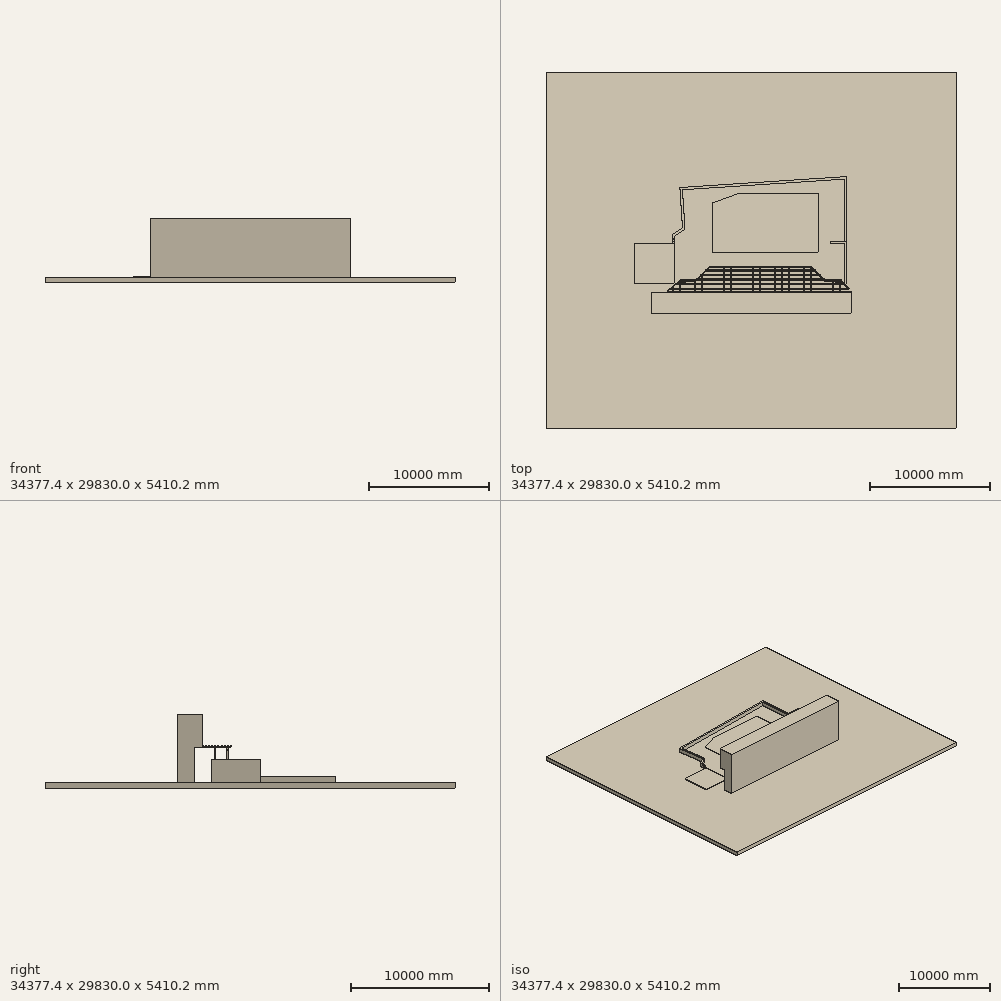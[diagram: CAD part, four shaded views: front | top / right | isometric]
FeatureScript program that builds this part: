
annotation { "Feature Type Name" : "Feature", "Feature Type Description" : "" }
export const myFeature = defineFeature(function(context is Context, id is Id, definition is map)
    precondition{}
    {
        {
            var Q0;
            Q0=qCreatedBy(makeId("Right.planeOp"),FACE);
            var sketch = newSketch(context, id + "F0", { "sketchPlane" : qUnion([Q0])});
            skLineSegment(sketch, "E0", {"start": v(0, 4953) * mm, "end": v(0, 0) * mm});
            skLineSegment(sketch, "E1", {"start": v(0, 4953) * mm, "end": v(1828.8, 4953) * mm});
            skLineSegment(sketch, "E2", {"start": v(1828.8, 4953) * mm, "end": v(1828.8, 2514.6) * mm});
            skLineSegment(sketch, "E3", {"start": v(1828.8, 2514.6) * mm, "end": v(1219.2, 2514.6) * mm});
            skLineSegment(sketch, "E4", {"start": v(1219.2, 2514.6) * mm, "end": v(1219.2, 0) * mm});
            skLineSegment(sketch, "E5", {"start": v(1219.2, 0) * mm, "end": v(0, 0) * mm});
            skSolve(sketch);
        }
        {
            var Q0;
            Q0 = qSketchRegion(id + "F0", true);
            extrude(context, id + "F1", {"entities" : qUnion([Q0]), "depth" : 16764 * mm, "offsetDistance" : 25.4 * mm});
        }
        {
            var Q0;
            Q0=qCreatedBy(makeId("Top.planeOp"),FACE);
            var sketch = newSketch(context, id + "F2", { "sketchPlane" : qUnion([Q0])});
            skLineSegment(sketch, "E6.bottom", {"start": v(-1422.4, 2540) * mm, "end": v(1930.4, 2540) * mm});
            skLineSegment(sketch, "E6.top", {"start": v(-1422.4, 5892.8) * mm, "end": v(1930.4, 5892.8) * mm});
            skLineSegment(sketch, "E6.left", {"start": v(-1422.4, 2540) * mm, "end": v(-1422.4, 5892.8) * mm});
            skLineSegment(sketch, "E6.right", {"start": v(1930.4, 2540) * mm, "end": v(1930.4, 5892.8) * mm});
            skSolve(sketch);
        }
        {
            var Q0;
            Q0 = qSketchRegion(id + "F2", true);
            extrude(context, id + "F3", {"entities" : qUnion([Q0]), "depth" : 76.2 * mm, "offsetDistance" : 25.4 * mm});
        }
        {
            var Q0;
            Q0=qCreatedBy(makeId("Top.planeOp"),FACE);
            var sketch = newSketch(context, id + "F4", { "sketchPlane" : qUnion([Q0])});
            skLineSegment(sketch, "E7", {"start": v(5130.8, 5130.8) * mm, "end": v(14020.8, 5130.8) * mm});
            skLineSegment(sketch, "E8", {"start": v(14020.8, 10109.2) * mm, "end": v(14020.8, 5130.8) * mm});
            skLineSegment(sketch, "E9", {"start": v(14020.8, 10109.2) * mm, "end": v(7375.8, 10109.2) * mm});
            skLineSegment(sketch, "E10", {"start": v(5130.8, 5130.8) * mm, "end": v(5130.8, 9296.4) * mm});
            skLineSegment(sketch, "E11", {"start": v(5130.8, 9296.4) * mm, "end": v(7375.8, 10109.2) * mm});
            skSolve(sketch);
        }
        {
            var Q0;
            Q0 = qSketchRegion(id + "F4", true);
            extrude(context, id + "F5", {"entities" : qUnion([Q0]), "depth" : 25.4 * mm, "offsetDistance" : 25.4 * mm});
        }
        {
            var Q0;
            Q0=qCreatedBy(makeId("Top.planeOp"),FACE);
            var sketch = newSketch(context, id + "F6", { "sketchPlane" : qUnion([Q0])});
            skLineSegment(sketch, "E12", {"start": v(15036.8, 6070.6) * mm, "end": v(15036.8, 5918.2) * mm});
            skLineSegment(sketch, "E13", {"start": v(15036.8, 5918.2) * mm, "end": v(16205.2, 5918.2) * mm});
            skLineSegment(sketch, "E14", {"start": v(16205.2, 5918.2) * mm, "end": v(16205.2, 2489.2) * mm});
            skLineSegment(sketch, "E15", {"start": v(16205.2, 2489.2) * mm, "end": v(16357.6, 2489.2) * mm});
            skLineSegment(sketch, "E16", {"start": v(16357.6, 2489.2) * mm, "end": v(16357.6, 6070.6) * mm});
            skLineSegment(sketch, "E17", {"start": v(16357.6, 6070.6) * mm, "end": v(15036.8, 6070.6) * mm});
            skSolve(sketch);
        }
        {
            var Q0;
            Q0 = qSketchRegion(id + "F6", true);
            extrude(context, id + "F7", {"entities" : qUnion([Q0]), "depth" : 1676.4 * mm, "offsetDistance" : 25.4 * mm});
        }
        {
            var Q0;
            Q0=qCreatedBy(makeId("Top.planeOp"),FACE);
            var sketch = newSketch(context, id + "F8", { "sketchPlane" : qUnion([Q0])});
            skLineSegment(sketch, "E18", {"start": v(1930.4, 5892.8) * mm, "end": v(1930.4, 6502.4) * mm});
            skLineSegment(sketch, "E19", {"start": v(1930.4, 6502.4) * mm, "end": v(2813.78, 7075.54) * mm});
            skLineSegment(sketch, "E20", {"start": v(2813.78, 7075.54) * mm, "end": v(2595.32, 10405.68) * mm});
            skLineSegment(sketch, "E21", {"start": v(2595.32, 10405.68) * mm, "end": v(16154.4, 11295.16) * mm});
            skLineSegment(sketch, "E22", {"start": v(16154.4, 11295.16) * mm, "end": v(16154.4, 6070.6) * mm});
            skLineSegment(sketch, "E23", {"start": v(16154.4, 6070.6) * mm, "end": v(16357.6, 6070.6) * mm});
            skLineSegment(sketch, "E24", {"start": v(16357.6, 6070.6) * mm, "end": v(16357.6, 11512.13) * mm});
            skLineSegment(sketch, "E25", {"start": v(16357.6, 11512.13) * mm, "end": v(2379.26, 10595.14) * mm});
            skLineSegment(sketch, "E26", {"start": v(2379.26, 10595.14) * mm, "end": v(2603.22, 7181.15) * mm});
            skLineSegment(sketch, "E27", {"start": v(2603.22, 7181.15) * mm, "end": v(1727.2, 6612.78) * mm});
            skLineSegment(sketch, "E28", {"start": v(1727.2, 6612.78) * mm, "end": v(1727.2, 5892.8) * mm});
            skLineSegment(sketch, "E29", {"start": v(1727.2, 5892.8) * mm, "end": v(1930.4, 5892.8) * mm});
            skSolve(sketch);
        }
        {
            var Q0;
            Q0 = qSketchRegion(id + "F8", true);
            extrude(context, id + "F9", {"entities" : qUnion([Q0]), "depth" : 457.2 * mm, "offsetDistance" : 25.4 * mm});
        }
        {
            var Q0;
            Q0=makeQuery(id+"F9.opExtrude","SWEPT_FACE",FACE,{"disambiguationData":[OSD([sQuery(id+"F8.wireOp",EDGE,"E18")])]});
            var sketch = newSketch(context, id + "F10", { "sketchPlane" : qUnion([Q0])});
            skLineSegment(sketch, "E30", {"start": v(5892.8, 114.3) * mm, "end": v(6045.2, 114.3) * mm});
            skLineSegment(sketch, "E31", {"start": v(6045.2, 114.3) * mm, "end": v(6045.2, 228.6) * mm});
            skLineSegment(sketch, "E32", {"start": v(6045.2, 228.6) * mm, "end": v(6197.6, 228.6) * mm});
            skLineSegment(sketch, "E33", {"start": v(6197.6, 228.6) * mm, "end": v(6197.6, 342.9) * mm});
            skLineSegment(sketch, "E34", {"start": v(6197.6, 342.9) * mm, "end": v(6350, 342.9) * mm});
            skLineSegment(sketch, "E35", {"start": v(6350, 342.9) * mm, "end": v(6350, 457.2) * mm});
            skLineSegment(sketch, "E36", {"start": v(6350, 457.2) * mm, "end": v(5892.8, 457.2) * mm});
            skLineSegment(sketch, "E37", {"start": v(5892.8, 457.2) * mm, "end": v(5892.8, 114.3) * mm});
            skSolve(sketch);
        }
        {
            var Q0;
            Q0 = qSketchRegion(id + "F10", true);
            extrude(context, id + "F11", {"entities" : qUnion([Q0]), "operationType" : NewBodyOperationType.REMOVE, "oppositeDirection" : true, "depth" : 203.2 * mm, "offsetDistance" : 25.4 * mm});
        }
        {
            var Q0;
            Q0=qCreatedBy(makeId("Top.planeOp"),FACE);
            var sketch = newSketch(context, id + "F12", { "sketchPlane" : qUnion([Q0])});
            skLineSegment(sketch, "E38.bottom", {"start": v(2590.8, 2667) * mm, "end": v(2692.4, 2667) * mm});
            skLineSegment(sketch, "E38.top", {"start": v(2590.8, 2768.6) * mm, "end": v(2692.4, 2768.6) * mm});
            skLineSegment(sketch, "E38.left", {"start": v(2590.8, 2667) * mm, "end": v(2590.8, 2768.6) * mm});
            skLineSegment(sketch, "E38.right", {"start": v(2692.4, 2667) * mm, "end": v(2692.4, 2768.6) * mm});
            skLineSegment(sketch, "E39.bottom", {"start": v(4826, 3581.4) * mm, "end": v(4927.6, 3581.4) * mm});
            skLineSegment(sketch, "E39.top", {"start": v(4826, 3683) * mm, "end": v(4927.6, 3683) * mm});
            skLineSegment(sketch, "E39.left", {"start": v(4826, 3683) * mm, "end": v(4826, 3581.4) * mm});
            skLineSegment(sketch, "E39.right", {"start": v(4927.6, 3683) * mm, "end": v(4927.6, 3581.4) * mm});
            skLineSegment(sketch, "E40.bottom", {"start": v(9093.2, 3683) * mm, "end": v(9194.8, 3683) * mm});
            skLineSegment(sketch, "E40.top", {"start": v(9093.2, 3581.4) * mm, "end": v(9194.8, 3581.4) * mm});
            skLineSegment(sketch, "E40.left", {"start": v(9093.2, 3683) * mm, "end": v(9093.2, 3581.4) * mm});
            skLineSegment(sketch, "E40.right", {"start": v(9194.8, 3683) * mm, "end": v(9194.8, 3581.4) * mm});
            skLineSegment(sketch, "E41", {"start": v(9144, 3250.57) * mm, "end": v(9144, 4336.45) * mm, "construction": true});
            skLineSegment(sketch, "E42.MirrorCS", {"start": v(13462, 3683) * mm, "end": v(13462, 3581.4) * mm});
            skLineSegment(sketch, "E43.MirrorCS", {"start": v(13360.4, 3683) * mm, "end": v(13360.4, 3581.4) * mm});
            skLineSegment(sketch, "E44.MirrorCS", {"start": v(13462, 3683) * mm, "end": v(13360.4, 3683) * mm});
            skLineSegment(sketch, "E45.MirrorCS", {"start": v(13462, 3581.4) * mm, "end": v(13360.4, 3581.4) * mm});
            skLineSegment(sketch, "E46.MirrorCS", {"start": v(15595.6, 2667) * mm, "end": v(15595.6, 2768.6) * mm});
            skLineSegment(sketch, "E47.MirrorCS", {"start": v(15697.2, 2768.6) * mm, "end": v(15595.6, 2768.6) * mm});
            skLineSegment(sketch, "E48.MirrorCS", {"start": v(15697.2, 2667) * mm, "end": v(15697.2, 2768.6) * mm});
            skLineSegment(sketch, "E49.MirrorCS", {"start": v(15697.2, 2667) * mm, "end": v(15595.6, 2667) * mm});
            skSolve(sketch);
        }
        {
            var Q0;
            Q0 = qSketchRegion(id + "F12", true);
            extrude(context, id + "F13", {"entities" : qUnion([Q0]), "depth" : 2336.8 * mm, "offsetDistance" : 25.4 * mm});
        }
        {
            var Q0;
            Q0=makeQuery(id+"F13.opExtrude","SWEPT_FACE",FACE,{"disambiguationData":[OSD([sQuery(id+"F12.wireOp",EDGE,"E40.bottom")])]});
            var sketch = newSketch(context, id + "F14", { "sketchPlane" : qUnion([Q0])});
            skLineSegment(sketch, "E50.bottom", {"start": v(-13665.2, 2514.6) * mm, "end": v(-4622.8, 2514.6) * mm});
            skLineSegment(sketch, "E50.top", {"start": v(-13576.3, 2336.8) * mm, "end": v(-4711.7, 2336.8) * mm});
            skLineSegment(sketch, "E50.left", {"start": v(-13665.2, 2514.6) * mm, "end": v(-13665.2, 2425.7) * mm});
            skLineSegment(sketch, "E50.right", {"start": v(-4622.8, 2514.6) * mm, "end": v(-4622.8, 2425.7) * mm});
            skLineSegment(sketch, "E51", {"start": v(-13665.2, 2425.7) * mm, "end": v(-13576.3, 2336.8) * mm});
            skPoint(sketch, "E52.orphan", {"position": v(-13665.2, 2336.8) * mm});
            skLineSegment(sketch, "E53", {"start": v(-4622.8, 2425.7) * mm, "end": v(-4711.7, 2336.8) * mm});
            skPoint(sketch, "E54.orphan", {"position": v(-4622.8, 2336.8) * mm});
            skSolve(sketch);
        }
        {
            var Q0;
            Q0 = qSketchRegion(id + "F14", true);
            extrude(context, id + "F15", {"entities" : qUnion([Q0]), "oppositeDirection" : true, "depth" : 101.6 * mm, "offsetDistance" : 25.4 * mm});
        }
        {
            var Q0;
            Q0=makeQuery(id+"F13.opExtrude","SWEPT_FACE",FACE,{"disambiguationData":[OSD([sQuery(id+"F12.wireOp",EDGE,"E38.top")])]});
            var sketch = newSketch(context, id + "F16", { "sketchPlane" : qUnion([Q0])});
            skLineSegment(sketch, "E55.bottom", {"start": v(-2895.6, 2514.6) * mm, "end": v(-2387.6, 2514.6) * mm});
            skLineSegment(sketch, "E55.top", {"start": v(-2806.7, 2336.8) * mm, "end": v(-2476.5, 2336.8) * mm});
            skLineSegment(sketch, "E55.left", {"start": v(-2895.6, 2514.6) * mm, "end": v(-2895.6, 2425.7) * mm});
            skLineSegment(sketch, "E55.right", {"start": v(-2387.6, 2514.6) * mm, "end": v(-2387.6, 2425.7) * mm});
            skLineSegment(sketch, "E56", {"start": v(-2895.6, 2425.7) * mm, "end": v(-2806.7, 2336.8) * mm});
            skLineSegment(sketch, "E57", {"start": v(-2387.6, 2425.7) * mm, "end": v(-2476.5, 2336.8) * mm});
            skPoint(sketch, "E58.orphan", {"position": v(-2895.6, 2336.8) * mm});
            skPoint(sketch, "E59.orphan", {"position": v(-2387.6, 2336.8) * mm});
            skLineSegment(sketch, "E60", {"start": v(-9144, 3615.2) * mm, "end": v(-9144, 519.06) * mm, "construction": true});
            skLineSegment(sketch, "E61.MirrorCS", {"start": v(-15392.4, 2514.6) * mm, "end": v(-15900.4, 2514.6) * mm});
            skLineSegment(sketch, "E62.MirrorCS", {"start": v(-15900.4, 2514.6) * mm, "end": v(-15900.4, 2425.7) * mm});
            skLineSegment(sketch, "E63.MirrorCS", {"start": v(-15900.4, 2425.7) * mm, "end": v(-15811.5, 2336.8) * mm});
            skLineSegment(sketch, "E64.MirrorCS", {"start": v(-15481.3, 2336.8) * mm, "end": v(-15811.5, 2336.8) * mm});
            skLineSegment(sketch, "E65.MirrorCS", {"start": v(-15392.4, 2425.7) * mm, "end": v(-15481.3, 2336.8) * mm});
            skLineSegment(sketch, "E66.MirrorCS", {"start": v(-15392.4, 2514.6) * mm, "end": v(-15392.4, 2425.7) * mm});
            skSolve(sketch);
        }
        {
            var Q0;
            Q0 = qSketchRegion(id + "F16", true);
            extrude(context, id + "F17", {"entities" : qUnion([Q0]), "oppositeDirection" : true, "depth" : 101.6 * mm, "offsetDistance" : 25.4 * mm});
        }
        {
            var Q0;
            Q0=makeQuery(id+"F1.opExtrude","SWEPT_FACE",FACE,{"disambiguationData":[OSD([sQuery(id+"F0.wireOp",EDGE,"E2")])]});
            var sketch = newSketch(context, id + "F18", { "sketchPlane" : qUnion([Q0])});
            skLineSegment(sketch, "E67.bottom", {"start": v(-16764, 2514.6) * mm, "end": v(-1320.8, 2514.6) * mm});
            skLineSegment(sketch, "E67.top", {"start": v(-16764, 2616.2) * mm, "end": v(-1320.8, 2616.2) * mm});
            skLineSegment(sketch, "E67.left", {"start": v(-16764, 2514.6) * mm, "end": v(-16764, 2616.2) * mm});
            skLineSegment(sketch, "E67.right", {"start": v(-1320.8, 2514.6) * mm, "end": v(-1320.8, 2616.2) * mm});
            skSolve(sketch);
        }
        {
            var Q0;
            Q0 = qSketchRegion(id + "F18", true);
            extrude(context, id + "F19", {"entities" : qUnion([Q0]), "operationType" : NewBodyOperationType.ADD, "depth" : 50.8 * mm, "offsetDistance" : 25.4 * mm});
        }
        {
            var Q0;
            Q0=makeQuery(id+"F15.opExtrude","SWEPT_FACE",FACE,{"disambiguationData":[OSD([sQuery(id+"F14.wireOp",EDGE,"E50.bottom")])]});
            var sketch = newSketch(context, id + "F20", { "sketchPlane" : qUnion([Q0])});
            skLineSegment(sketch, "E68", {"start": v(1320.8, 1879.6) * mm, "end": v(2387.6, 2768.6) * mm});
            skLineSegment(sketch, "E69", {"start": v(2387.6, 2768.6) * mm, "end": v(3708.4, 2768.6) * mm});
            skLineSegment(sketch, "E70", {"start": v(3708.4, 2768.6) * mm, "end": v(4902.2, 3962.4) * mm});
            skLineSegment(sketch, "E71", {"start": v(4902.2, 3962.4) * mm, "end": v(13385.8, 3962.4) * mm});
            skLineSegment(sketch, "E72", {"start": v(13385.8, 3962.4) * mm, "end": v(14579.6, 2768.6) * mm});
            skLineSegment(sketch, "E73", {"start": v(14579.6, 2768.6) * mm, "end": v(15900.4, 2768.6) * mm});
            skLineSegment(sketch, "E74", {"start": v(15900.4, 2768.6) * mm, "end": v(16764, 1879.6) * mm});
            skLineSegment(sketch, "E75", {"start": v(1320.8, 1879.6) * mm, "end": v(1400.15, 1879.6) * mm});
            skLineSegment(sketch, "E76", {"start": v(1400.15, 1879.6) * mm, "end": v(2406, 2717.8) * mm});
            skLineSegment(sketch, "E77", {"start": v(2406, 2717.8) * mm, "end": v(3729.44, 2717.8) * mm});
            skLineSegment(sketch, "E78", {"start": v(3729.44, 2717.8) * mm, "end": v(4923.24, 3911.6) * mm});
            skLineSegment(sketch, "E79", {"start": v(4923.24, 3911.6) * mm, "end": v(13364.76, 3911.6) * mm});
            skLineSegment(sketch, "E80", {"start": v(13364.76, 3911.6) * mm, "end": v(14558.56, 2717.8) * mm});
            skLineSegment(sketch, "E81", {"start": v(14558.56, 2717.8) * mm, "end": v(15878.93, 2717.8) * mm});
            skLineSegment(sketch, "E82", {"start": v(15878.93, 2717.8) * mm, "end": v(16693.18, 1879.6) * mm});
            skLineSegment(sketch, "E83", {"start": v(16693.18, 1879.6) * mm, "end": v(16764, 1879.6) * mm});
            skSolve(sketch);
        }
        {
            var Q0;
            Q0 = qSketchRegion(id + "F20", true);
            extrude(context, id + "F21", {"entities" : qUnion([Q0]), "depth" : 101.6 * mm, "offsetDistance" : 25.4 * mm});
        }
        {
            var Q0;
            Q0=makeQuery(id+"F19.opExtrude","CAP_FACE",FACE,{"disambiguationData":[OSD([sQuery(id+"F18.wireOp",EDGE,"E67.bottom"),sQuery(id+"F18.wireOp",EDGE,"E67.top"),sQuery(id+"F18.wireOp",EDGE,"E67.left"),sQuery(id+"F18.wireOp",EDGE,"E67.right")])],"isStart":false});
            var sketch = newSketch(context, id + "F22", { "sketchPlane" : qUnion([Q0])});
            skLineSegment(sketch, "E84.bottom", {"start": v(-1828.8, 2616.2) * mm, "end": v(-1778, 2616.2) * mm});
            skLineSegment(sketch, "E84.top", {"start": v(-1828.8, 2514.6) * mm, "end": v(-1778, 2514.6) * mm});
            skLineSegment(sketch, "E84.left", {"start": v(-1828.8, 2616.2) * mm, "end": v(-1828.8, 2514.6) * mm});
            skLineSegment(sketch, "E84.right", {"start": v(-1778, 2616.2) * mm, "end": v(-1778, 2514.6) * mm});
            skLineSegment(sketch, "E85.1.0.0", {"start": v(-2438.4, 2616.2) * mm, "end": v(-2438.4, 2514.6) * mm});
            skLineSegment(sketch, "E85.1.0.1", {"start": v(-2387.6, 2616.2) * mm, "end": v(-2387.6, 2514.6) * mm});
            skLineSegment(sketch, "E85.1.0.2", {"start": v(-2438.4, 2616.2) * mm, "end": v(-2387.6, 2616.2) * mm});
            skLineSegment(sketch, "E85.1.0.3", {"start": v(-2438.4, 2514.6) * mm, "end": v(-2387.6, 2514.6) * mm});
            skLineSegment(sketch, "E85.2.0.0", {"start": v(-3048, 2616.2) * mm, "end": v(-3048, 2514.6) * mm});
            skLineSegment(sketch, "E85.2.0.1", {"start": v(-2997.2, 2616.2) * mm, "end": v(-2997.2, 2514.6) * mm});
            skLineSegment(sketch, "E85.2.0.2", {"start": v(-3048, 2616.2) * mm, "end": v(-2997.2, 2616.2) * mm});
            skLineSegment(sketch, "E85.2.0.3", {"start": v(-3048, 2514.6) * mm, "end": v(-2997.2, 2514.6) * mm});
            skLineSegment(sketch, "E85.3.0.0", {"start": v(-3657.6, 2616.2) * mm, "end": v(-3657.6, 2514.6) * mm});
            skLineSegment(sketch, "E85.3.0.1", {"start": v(-3606.8, 2616.2) * mm, "end": v(-3606.8, 2514.6) * mm});
            skLineSegment(sketch, "E85.3.0.2", {"start": v(-3657.6, 2616.2) * mm, "end": v(-3606.8, 2616.2) * mm});
            skLineSegment(sketch, "E85.3.0.3", {"start": v(-3657.6, 2514.6) * mm, "end": v(-3606.8, 2514.6) * mm});
            skLineSegment(sketch, "E85.4.0.0", {"start": v(-4267.2, 2616.2) * mm, "end": v(-4267.2, 2514.6) * mm});
            skLineSegment(sketch, "E85.4.0.1", {"start": v(-4216.4, 2616.2) * mm, "end": v(-4216.4, 2514.6) * mm});
            skLineSegment(sketch, "E85.4.0.2", {"start": v(-4267.2, 2616.2) * mm, "end": v(-4216.4, 2616.2) * mm});
            skLineSegment(sketch, "E85.4.0.3", {"start": v(-4267.2, 2514.6) * mm, "end": v(-4216.4, 2514.6) * mm});
            skLineSegment(sketch, "E85.5.0.0", {"start": v(-4876.8, 2616.2) * mm, "end": v(-4876.8, 2514.6) * mm});
            skLineSegment(sketch, "E85.5.0.1", {"start": v(-4826, 2616.2) * mm, "end": v(-4826, 2514.6) * mm});
            skLineSegment(sketch, "E85.5.0.2", {"start": v(-4876.8, 2616.2) * mm, "end": v(-4826, 2616.2) * mm});
            skLineSegment(sketch, "E85.5.0.3", {"start": v(-4876.8, 2514.6) * mm, "end": v(-4826, 2514.6) * mm});
            skLineSegment(sketch, "E85.6.0.0", {"start": v(-5486.4, 2616.2) * mm, "end": v(-5486.4, 2514.6) * mm});
            skLineSegment(sketch, "E85.6.0.1", {"start": v(-5435.6, 2616.2) * mm, "end": v(-5435.6, 2514.6) * mm});
            skLineSegment(sketch, "E85.6.0.2", {"start": v(-5486.4, 2616.2) * mm, "end": v(-5435.6, 2616.2) * mm});
            skLineSegment(sketch, "E85.6.0.3", {"start": v(-5486.4, 2514.6) * mm, "end": v(-5435.6, 2514.6) * mm});
            skLineSegment(sketch, "E85.7.0.0", {"start": v(-6096, 2616.2) * mm, "end": v(-6096, 2514.6) * mm});
            skLineSegment(sketch, "E85.7.0.1", {"start": v(-6045.2, 2616.2) * mm, "end": v(-6045.2, 2514.6) * mm});
            skLineSegment(sketch, "E85.7.0.2", {"start": v(-6096, 2616.2) * mm, "end": v(-6045.2, 2616.2) * mm});
            skLineSegment(sketch, "E85.7.0.3", {"start": v(-6096, 2514.6) * mm, "end": v(-6045.2, 2514.6) * mm});
            skLineSegment(sketch, "E85.8.0.0", {"start": v(-6705.6, 2616.2) * mm, "end": v(-6705.6, 2514.6) * mm});
            skLineSegment(sketch, "E85.8.0.1", {"start": v(-6654.8, 2616.2) * mm, "end": v(-6654.8, 2514.6) * mm});
            skLineSegment(sketch, "E85.8.0.2", {"start": v(-6705.6, 2616.2) * mm, "end": v(-6654.8, 2616.2) * mm});
            skLineSegment(sketch, "E85.8.0.3", {"start": v(-6705.6, 2514.6) * mm, "end": v(-6654.8, 2514.6) * mm});
            skLineSegment(sketch, "E85.9.0.0", {"start": v(-7315.2, 2616.2) * mm, "end": v(-7315.2, 2514.6) * mm});
            skLineSegment(sketch, "E85.9.0.1", {"start": v(-7264.4, 2616.2) * mm, "end": v(-7264.4, 2514.6) * mm});
            skLineSegment(sketch, "E85.9.0.2", {"start": v(-7315.2, 2616.2) * mm, "end": v(-7264.4, 2616.2) * mm});
            skLineSegment(sketch, "E85.9.0.3", {"start": v(-7315.2, 2514.6) * mm, "end": v(-7264.4, 2514.6) * mm});
            skLineSegment(sketch, "E85.10.0.0", {"start": v(-7924.8, 2616.2) * mm, "end": v(-7924.8, 2514.6) * mm});
            skLineSegment(sketch, "E85.10.0.1", {"start": v(-7874, 2616.2) * mm, "end": v(-7874, 2514.6) * mm});
            skLineSegment(sketch, "E85.10.0.2", {"start": v(-7924.8, 2616.2) * mm, "end": v(-7874, 2616.2) * mm});
            skLineSegment(sketch, "E85.10.0.3", {"start": v(-7924.8, 2514.6) * mm, "end": v(-7874, 2514.6) * mm});
            skLineSegment(sketch, "E85.11.0.0", {"start": v(-8534.4, 2616.2) * mm, "end": v(-8534.4, 2514.6) * mm});
            skLineSegment(sketch, "E85.11.0.1", {"start": v(-8483.6, 2616.2) * mm, "end": v(-8483.6, 2514.6) * mm});
            skLineSegment(sketch, "E85.11.0.2", {"start": v(-8534.4, 2616.2) * mm, "end": v(-8483.6, 2616.2) * mm});
            skLineSegment(sketch, "E85.11.0.3", {"start": v(-8534.4, 2514.6) * mm, "end": v(-8483.6, 2514.6) * mm});
            skLineSegment(sketch, "E85.12.0.0", {"start": v(-9144, 2616.2) * mm, "end": v(-9144, 2514.6) * mm});
            skLineSegment(sketch, "E85.12.0.1", {"start": v(-9093.2, 2616.2) * mm, "end": v(-9093.2, 2514.6) * mm});
            skLineSegment(sketch, "E85.12.0.2", {"start": v(-9144, 2616.2) * mm, "end": v(-9093.2, 2616.2) * mm});
            skLineSegment(sketch, "E85.12.0.3", {"start": v(-9144, 2514.6) * mm, "end": v(-9093.2, 2514.6) * mm});
            skLineSegment(sketch, "E85.13.0.0", {"start": v(-9753.6, 2616.2) * mm, "end": v(-9753.6, 2514.6) * mm});
            skLineSegment(sketch, "E85.13.0.1", {"start": v(-9702.8, 2616.2) * mm, "end": v(-9702.8, 2514.6) * mm});
            skLineSegment(sketch, "E85.13.0.2", {"start": v(-9753.6, 2616.2) * mm, "end": v(-9702.8, 2616.2) * mm});
            skLineSegment(sketch, "E85.13.0.3", {"start": v(-9753.6, 2514.6) * mm, "end": v(-9702.8, 2514.6) * mm});
            skLineSegment(sketch, "E85.14.0.0", {"start": v(-10363.2, 2616.2) * mm, "end": v(-10363.2, 2514.6) * mm});
            skLineSegment(sketch, "E85.14.0.1", {"start": v(-10312.4, 2616.2) * mm, "end": v(-10312.4, 2514.6) * mm});
            skLineSegment(sketch, "E85.14.0.2", {"start": v(-10363.2, 2616.2) * mm, "end": v(-10312.4, 2616.2) * mm});
            skLineSegment(sketch, "E85.14.0.3", {"start": v(-10363.2, 2514.6) * mm, "end": v(-10312.4, 2514.6) * mm});
            skLineSegment(sketch, "E85.15.0.0", {"start": v(-10972.8, 2616.2) * mm, "end": v(-10972.8, 2514.6) * mm});
            skLineSegment(sketch, "E85.15.0.1", {"start": v(-10922, 2616.2) * mm, "end": v(-10922, 2514.6) * mm});
            skLineSegment(sketch, "E85.15.0.2", {"start": v(-10972.8, 2616.2) * mm, "end": v(-10922, 2616.2) * mm});
            skLineSegment(sketch, "E85.15.0.3", {"start": v(-10972.8, 2514.6) * mm, "end": v(-10922, 2514.6) * mm});
            skLineSegment(sketch, "E85.16.0.0", {"start": v(-11582.4, 2616.2) * mm, "end": v(-11582.4, 2514.6) * mm});
            skLineSegment(sketch, "E85.16.0.1", {"start": v(-11531.6, 2616.2) * mm, "end": v(-11531.6, 2514.6) * mm});
            skLineSegment(sketch, "E85.16.0.2", {"start": v(-11582.4, 2616.2) * mm, "end": v(-11531.6, 2616.2) * mm});
            skLineSegment(sketch, "E85.16.0.3", {"start": v(-11582.4, 2514.6) * mm, "end": v(-11531.6, 2514.6) * mm});
            skLineSegment(sketch, "E85.17.0.0", {"start": v(-12192, 2616.2) * mm, "end": v(-12192, 2514.6) * mm});
            skLineSegment(sketch, "E85.17.0.1", {"start": v(-12141.2, 2616.2) * mm, "end": v(-12141.2, 2514.6) * mm});
            skLineSegment(sketch, "E85.17.0.2", {"start": v(-12192, 2616.2) * mm, "end": v(-12141.2, 2616.2) * mm});
            skLineSegment(sketch, "E85.17.0.3", {"start": v(-12192, 2514.6) * mm, "end": v(-12141.2, 2514.6) * mm});
            skLineSegment(sketch, "E85.18.0.0", {"start": v(-12801.6, 2616.2) * mm, "end": v(-12801.6, 2514.6) * mm});
            skLineSegment(sketch, "E85.18.0.1", {"start": v(-12750.8, 2616.2) * mm, "end": v(-12750.8, 2514.6) * mm});
            skLineSegment(sketch, "E85.18.0.2", {"start": v(-12801.6, 2616.2) * mm, "end": v(-12750.8, 2616.2) * mm});
            skLineSegment(sketch, "E85.18.0.3", {"start": v(-12801.6, 2514.6) * mm, "end": v(-12750.8, 2514.6) * mm});
            skLineSegment(sketch, "E85.19.0.0", {"start": v(-13411.2, 2616.2) * mm, "end": v(-13411.2, 2514.6) * mm});
            skLineSegment(sketch, "E85.19.0.1", {"start": v(-13360.4, 2616.2) * mm, "end": v(-13360.4, 2514.6) * mm});
            skLineSegment(sketch, "E85.19.0.2", {"start": v(-13411.2, 2616.2) * mm, "end": v(-13360.4, 2616.2) * mm});
            skLineSegment(sketch, "E85.19.0.3", {"start": v(-13411.2, 2514.6) * mm, "end": v(-13360.4, 2514.6) * mm});
            skLineSegment(sketch, "E85.20.0.0", {"start": v(-14020.8, 2616.2) * mm, "end": v(-14020.8, 2514.6) * mm});
            skLineSegment(sketch, "E85.20.0.1", {"start": v(-13970, 2616.2) * mm, "end": v(-13970, 2514.6) * mm});
            skLineSegment(sketch, "E85.20.0.2", {"start": v(-14020.8, 2616.2) * mm, "end": v(-13970, 2616.2) * mm});
            skLineSegment(sketch, "E85.20.0.3", {"start": v(-14020.8, 2514.6) * mm, "end": v(-13970, 2514.6) * mm});
            skLineSegment(sketch, "E85.21.0.0", {"start": v(-14630.4, 2616.2) * mm, "end": v(-14630.4, 2514.6) * mm});
            skLineSegment(sketch, "E85.21.0.1", {"start": v(-14579.6, 2616.2) * mm, "end": v(-14579.6, 2514.6) * mm});
            skLineSegment(sketch, "E85.21.0.2", {"start": v(-14630.4, 2616.2) * mm, "end": v(-14579.6, 2616.2) * mm});
            skLineSegment(sketch, "E85.21.0.3", {"start": v(-14630.4, 2514.6) * mm, "end": v(-14579.6, 2514.6) * mm});
            skLineSegment(sketch, "E85.22.0.0", {"start": v(-15240, 2616.2) * mm, "end": v(-15240, 2514.6) * mm});
            skLineSegment(sketch, "E85.22.0.1", {"start": v(-15189.2, 2616.2) * mm, "end": v(-15189.2, 2514.6) * mm});
            skLineSegment(sketch, "E85.22.0.2", {"start": v(-15240, 2616.2) * mm, "end": v(-15189.2, 2616.2) * mm});
            skLineSegment(sketch, "E85.22.0.3", {"start": v(-15240, 2514.6) * mm, "end": v(-15189.2, 2514.6) * mm});
            skLineSegment(sketch, "E85.23.0.0", {"start": v(-15849.6, 2616.2) * mm, "end": v(-15849.6, 2514.6) * mm});
            skLineSegment(sketch, "E85.23.0.1", {"start": v(-15798.8, 2616.2) * mm, "end": v(-15798.8, 2514.6) * mm});
            skLineSegment(sketch, "E85.23.0.2", {"start": v(-15849.6, 2616.2) * mm, "end": v(-15798.8, 2616.2) * mm});
            skLineSegment(sketch, "E85.23.0.3", {"start": v(-15849.6, 2514.6) * mm, "end": v(-15798.8, 2514.6) * mm});
            skLineSegment(sketch, "E85.24.0.0", {"start": v(-16459.2, 2616.2) * mm, "end": v(-16459.2, 2514.6) * mm});
            skLineSegment(sketch, "E85.24.0.1", {"start": v(-16408.4, 2616.2) * mm, "end": v(-16408.4, 2514.6) * mm});
            skLineSegment(sketch, "E85.24.0.2", {"start": v(-16459.2, 2616.2) * mm, "end": v(-16408.4, 2616.2) * mm});
            skLineSegment(sketch, "E85.24.0.3", {"start": v(-16459.2, 2514.6) * mm, "end": v(-16408.4, 2514.6) * mm});
            skLineSegment(sketch, "E85.direction1", {"start": v(-1828.8, 2514.6) * mm, "end": v(-2438.4, 2514.6) * mm, "construction": true});
            skSolve(sketch);
        }
        {
            var Q0;
            Q0 = qSketchRegion(id + "F22", true);
            extrude(context, id + "F23", {"entities" : qUnion([Q0]), "endBound" : BoundingType.UP_TO_NEXT, "depth" : 25.4 * mm, "offsetDistance" : 25.4 * mm});
        }
        {
            var Q0;
            Q0=makeQuery(id+"F19.boolean.opBoolean","MERGE",FACE,{"derivedFrom":[makeQuery(id+"F1.opExtrude","CAP_FACE",FACE,{"disambiguationData":[OSD([sQuery(id+"F0.wireOp",EDGE,"E0"),sQuery(id+"F0.wireOp",EDGE,"E1"),sQuery(id+"F0.wireOp",EDGE,"E2"),sQuery(id+"F0.wireOp",EDGE,"E3"),sQuery(id+"F0.wireOp",EDGE,"E4"),sQuery(id+"F0.wireOp",EDGE,"E5")])],"isStart":false}),makeQuery(id+"F19.opExtrude","SWEPT_FACE",FACE,{"disambiguationData":[OSD([sQuery(id+"F18.wireOp",EDGE,"E67.left")])]})]});
            var sketch = newSketch(context, id + "F24", { "sketchPlane" : qUnion([Q0])});
            skLineSegment(sketch, "E86.bottom", {"start": v(1854.2, 2667) * mm, "end": v(1884.68, 2667) * mm});
            skLineSegment(sketch, "E86.top", {"start": v(1854.2, 2616.2) * mm, "end": v(1884.68, 2616.2) * mm});
            skLineSegment(sketch, "E86.left", {"start": v(1854.2, 2667) * mm, "end": v(1854.2, 2616.2) * mm});
            skLineSegment(sketch, "E86.right", {"start": v(1884.68, 2667) * mm, "end": v(1884.68, 2616.2) * mm});
            skLineSegment(sketch, "E87.1.0.0", {"start": v(1960.88, 2616.2) * mm, "end": v(1991.36, 2616.2) * mm});
            skLineSegment(sketch, "E87.1.0.1", {"start": v(1991.36, 2667) * mm, "end": v(1991.36, 2616.2) * mm});
            skLineSegment(sketch, "E87.1.0.2", {"start": v(1960.88, 2667) * mm, "end": v(1991.36, 2667) * mm});
            skLineSegment(sketch, "E87.1.0.3", {"start": v(1960.88, 2667) * mm, "end": v(1960.88, 2616.2) * mm});
            skLineSegment(sketch, "E87.2.0.0", {"start": v(2067.56, 2616.2) * mm, "end": v(2098.04, 2616.2) * mm});
            skLineSegment(sketch, "E87.2.0.1", {"start": v(2098.04, 2667) * mm, "end": v(2098.04, 2616.2) * mm});
            skLineSegment(sketch, "E87.2.0.2", {"start": v(2067.56, 2667) * mm, "end": v(2098.04, 2667) * mm});
            skLineSegment(sketch, "E87.2.0.3", {"start": v(2067.56, 2667) * mm, "end": v(2067.56, 2616.2) * mm});
            skLineSegment(sketch, "E87.3.0.0", {"start": v(2174.24, 2616.2) * mm, "end": v(2204.72, 2616.2) * mm});
            skLineSegment(sketch, "E87.3.0.1", {"start": v(2204.72, 2667) * mm, "end": v(2204.72, 2616.2) * mm});
            skLineSegment(sketch, "E87.3.0.2", {"start": v(2174.24, 2667) * mm, "end": v(2204.72, 2667) * mm});
            skLineSegment(sketch, "E87.3.0.3", {"start": v(2174.24, 2667) * mm, "end": v(2174.24, 2616.2) * mm});
            skLineSegment(sketch, "E87.4.0.0", {"start": v(2280.92, 2616.2) * mm, "end": v(2311.4, 2616.2) * mm});
            skLineSegment(sketch, "E87.4.0.1", {"start": v(2311.4, 2667) * mm, "end": v(2311.4, 2616.2) * mm});
            skLineSegment(sketch, "E87.4.0.2", {"start": v(2280.92, 2667) * mm, "end": v(2311.4, 2667) * mm});
            skLineSegment(sketch, "E87.4.0.3", {"start": v(2280.92, 2667) * mm, "end": v(2280.92, 2616.2) * mm});
            skLineSegment(sketch, "E87.5.0.0", {"start": v(2387.6, 2616.2) * mm, "end": v(2418.08, 2616.2) * mm});
            skLineSegment(sketch, "E87.5.0.1", {"start": v(2418.08, 2667) * mm, "end": v(2418.08, 2616.2) * mm});
            skLineSegment(sketch, "E87.5.0.2", {"start": v(2387.6, 2667) * mm, "end": v(2418.08, 2667) * mm});
            skLineSegment(sketch, "E87.5.0.3", {"start": v(2387.6, 2667) * mm, "end": v(2387.6, 2616.2) * mm});
            skLineSegment(sketch, "E87.6.0.0", {"start": v(2494.28, 2616.2) * mm, "end": v(2524.76, 2616.2) * mm});
            skLineSegment(sketch, "E87.6.0.1", {"start": v(2524.76, 2667) * mm, "end": v(2524.76, 2616.2) * mm});
            skLineSegment(sketch, "E87.6.0.2", {"start": v(2494.28, 2667) * mm, "end": v(2524.76, 2667) * mm});
            skLineSegment(sketch, "E87.6.0.3", {"start": v(2494.28, 2667) * mm, "end": v(2494.28, 2616.2) * mm});
            skLineSegment(sketch, "E87.7.0.0", {"start": v(2600.96, 2616.2) * mm, "end": v(2631.44, 2616.2) * mm});
            skLineSegment(sketch, "E87.7.0.1", {"start": v(2631.44, 2667) * mm, "end": v(2631.44, 2616.2) * mm});
            skLineSegment(sketch, "E87.7.0.2", {"start": v(2600.96, 2667) * mm, "end": v(2631.44, 2667) * mm});
            skLineSegment(sketch, "E87.7.0.3", {"start": v(2600.96, 2667) * mm, "end": v(2600.96, 2616.2) * mm});
            skLineSegment(sketch, "E87.8.0.0", {"start": v(2707.64, 2616.2) * mm, "end": v(2738.12, 2616.2) * mm});
            skLineSegment(sketch, "E87.8.0.1", {"start": v(2738.12, 2667) * mm, "end": v(2738.12, 2616.2) * mm});
            skLineSegment(sketch, "E87.8.0.2", {"start": v(2707.64, 2667) * mm, "end": v(2738.12, 2667) * mm});
            skLineSegment(sketch, "E87.8.0.3", {"start": v(2707.64, 2667) * mm, "end": v(2707.64, 2616.2) * mm});
            skLineSegment(sketch, "E87.9.0.0", {"start": v(2814.32, 2616.2) * mm, "end": v(2844.8, 2616.2) * mm});
            skLineSegment(sketch, "E87.9.0.1", {"start": v(2844.8, 2667) * mm, "end": v(2844.8, 2616.2) * mm});
            skLineSegment(sketch, "E87.9.0.2", {"start": v(2814.32, 2667) * mm, "end": v(2844.8, 2667) * mm});
            skLineSegment(sketch, "E87.9.0.3", {"start": v(2814.32, 2667) * mm, "end": v(2814.32, 2616.2) * mm});
            skLineSegment(sketch, "E87.10.0.0", {"start": v(2921, 2616.2) * mm, "end": v(2951.48, 2616.2) * mm});
            skLineSegment(sketch, "E87.10.0.1", {"start": v(2951.48, 2667) * mm, "end": v(2951.48, 2616.2) * mm});
            skLineSegment(sketch, "E87.10.0.2", {"start": v(2921, 2667) * mm, "end": v(2951.48, 2667) * mm});
            skLineSegment(sketch, "E87.10.0.3", {"start": v(2921, 2667) * mm, "end": v(2921, 2616.2) * mm});
            skLineSegment(sketch, "E87.11.0.0", {"start": v(3027.68, 2616.2) * mm, "end": v(3058.16, 2616.2) * mm});
            skLineSegment(sketch, "E87.11.0.1", {"start": v(3058.16, 2667) * mm, "end": v(3058.16, 2616.2) * mm});
            skLineSegment(sketch, "E87.11.0.2", {"start": v(3027.68, 2667) * mm, "end": v(3058.16, 2667) * mm});
            skLineSegment(sketch, "E87.11.0.3", {"start": v(3027.68, 2667) * mm, "end": v(3027.68, 2616.2) * mm});
            skLineSegment(sketch, "E87.12.0.0", {"start": v(3134.36, 2616.2) * mm, "end": v(3164.84, 2616.2) * mm});
            skLineSegment(sketch, "E87.12.0.1", {"start": v(3164.84, 2667) * mm, "end": v(3164.84, 2616.2) * mm});
            skLineSegment(sketch, "E87.12.0.2", {"start": v(3134.36, 2667) * mm, "end": v(3164.84, 2667) * mm});
            skLineSegment(sketch, "E87.12.0.3", {"start": v(3134.36, 2667) * mm, "end": v(3134.36, 2616.2) * mm});
            skLineSegment(sketch, "E87.13.0.0", {"start": v(3241.04, 2616.2) * mm, "end": v(3271.52, 2616.2) * mm});
            skLineSegment(sketch, "E87.13.0.1", {"start": v(3271.52, 2667) * mm, "end": v(3271.52, 2616.2) * mm});
            skLineSegment(sketch, "E87.13.0.2", {"start": v(3241.04, 2667) * mm, "end": v(3271.52, 2667) * mm});
            skLineSegment(sketch, "E87.13.0.3", {"start": v(3241.04, 2667) * mm, "end": v(3241.04, 2616.2) * mm});
            skLineSegment(sketch, "E87.14.0.0", {"start": v(3347.72, 2616.2) * mm, "end": v(3378.2, 2616.2) * mm});
            skLineSegment(sketch, "E87.14.0.1", {"start": v(3378.2, 2667) * mm, "end": v(3378.2, 2616.2) * mm});
            skLineSegment(sketch, "E87.14.0.2", {"start": v(3347.72, 2667) * mm, "end": v(3378.2, 2667) * mm});
            skLineSegment(sketch, "E87.14.0.3", {"start": v(3347.72, 2667) * mm, "end": v(3347.72, 2616.2) * mm});
            skLineSegment(sketch, "E87.15.0.0", {"start": v(3454.4, 2616.2) * mm, "end": v(3484.88, 2616.2) * mm});
            skLineSegment(sketch, "E87.15.0.1", {"start": v(3484.88, 2667) * mm, "end": v(3484.88, 2616.2) * mm});
            skLineSegment(sketch, "E87.15.0.2", {"start": v(3454.4, 2667) * mm, "end": v(3484.88, 2667) * mm});
            skLineSegment(sketch, "E87.15.0.3", {"start": v(3454.4, 2667) * mm, "end": v(3454.4, 2616.2) * mm});
            skLineSegment(sketch, "E87.16.0.0", {"start": v(3561.08, 2616.2) * mm, "end": v(3591.56, 2616.2) * mm});
            skLineSegment(sketch, "E87.16.0.1", {"start": v(3591.56, 2667) * mm, "end": v(3591.56, 2616.2) * mm});
            skLineSegment(sketch, "E87.16.0.2", {"start": v(3561.08, 2667) * mm, "end": v(3591.56, 2667) * mm});
            skLineSegment(sketch, "E87.16.0.3", {"start": v(3561.08, 2667) * mm, "end": v(3561.08, 2616.2) * mm});
            skLineSegment(sketch, "E87.17.0.0", {"start": v(3667.76, 2616.2) * mm, "end": v(3698.24, 2616.2) * mm});
            skLineSegment(sketch, "E87.17.0.1", {"start": v(3698.24, 2667) * mm, "end": v(3698.24, 2616.2) * mm});
            skLineSegment(sketch, "E87.17.0.2", {"start": v(3667.76, 2667) * mm, "end": v(3698.24, 2667) * mm});
            skLineSegment(sketch, "E87.17.0.3", {"start": v(3667.76, 2667) * mm, "end": v(3667.76, 2616.2) * mm});
            skLineSegment(sketch, "E87.18.0.0", {"start": v(3774.44, 2616.2) * mm, "end": v(3804.92, 2616.2) * mm});
            skLineSegment(sketch, "E87.18.0.1", {"start": v(3804.92, 2667) * mm, "end": v(3804.92, 2616.2) * mm});
            skLineSegment(sketch, "E87.18.0.2", {"start": v(3774.44, 2667) * mm, "end": v(3804.92, 2667) * mm});
            skLineSegment(sketch, "E87.18.0.3", {"start": v(3774.44, 2667) * mm, "end": v(3774.44, 2616.2) * mm});
            skLineSegment(sketch, "E87.19.0.0", {"start": v(3881.12, 2616.2) * mm, "end": v(3911.6, 2616.2) * mm});
            skLineSegment(sketch, "E87.19.0.1", {"start": v(3911.6, 2667) * mm, "end": v(3911.6, 2616.2) * mm});
            skLineSegment(sketch, "E87.19.0.2", {"start": v(3881.12, 2667) * mm, "end": v(3911.6, 2667) * mm});
            skLineSegment(sketch, "E87.19.0.3", {"start": v(3881.12, 2667) * mm, "end": v(3881.12, 2616.2) * mm});
            skLineSegment(sketch, "E87.direction1", {"start": v(1854.2, 2616.2) * mm, "end": v(1960.88, 2616.2) * mm, "construction": true});
            skSolve(sketch);
        }
        {
            var Q0;
            Q0 = qSketchRegion(id + "F24", true);
            var Q1;
            Q1=makeQuery(id+"F19.opExtrude","SWEPT_FACE",FACE,{"disambiguationData":[OSD([sQuery(id+"F18.wireOp",EDGE,"E67.right")])]});
            extrude(context, id + "F25", {"entities" : qUnion([Q0]), "endBound" : BoundingType.UP_TO_SURFACE, "oppositeDirection" : true, "depth" : 25.4 * mm, "endBoundEntityFace" : qUnion([Q1]), "offsetDistance" : 25.4 * mm});
        }
        {
            var Q0;
            Q0=makeQuery(id+"F25.opExtrude","SWEPT_FACE",FACE,{"disambiguationData":[OSD([sQuery(id+"F24.wireOp",EDGE,"E87.1.0.0")])]});
            var sketch = newSketch(context, id + "F26", { "sketchPlane" : qUnion([Q0])});
            skLineSegment(sketch, "E88", {"start": v(17152.03, -1553.06) * mm, "end": v(15897.2, -2844.8) * mm});
            skLineSegment(sketch, "E89", {"start": v(15897.2, -2844.8) * mm, "end": v(14575.24, -2844.8) * mm});
            skLineSegment(sketch, "E90", {"start": v(14575.24, -2844.8) * mm, "end": v(13197.48, -4222.57) * mm});
            skLineSegment(sketch, "E91", {"start": v(13197.48, -4222.57) * mm, "end": v(5090.52, -4222.57) * mm});
            skLineSegment(sketch, "E92", {"start": v(5090.52, -4222.57) * mm, "end": v(3712.76, -2844.8) * mm});
            skLineSegment(sketch, "E93", {"start": v(3712.76, -2844.8) * mm, "end": v(2399.69, -2844.8) * mm});
            skLineSegment(sketch, "E94", {"start": v(2399.69, -2844.8) * mm, "end": v(1180.49, -1828.8) * mm});
            skLineSegment(sketch, "E95", {"start": v(1180.49, -1828.8) * mm, "end": v(1180.49, -5801.32) * mm});
            skLineSegment(sketch, "E96", {"start": v(1180.49, -5801.32) * mm, "end": v(17152.03, -5801.32) * mm});
            skLineSegment(sketch, "E97", {"start": v(17152.03, -5801.32) * mm, "end": v(17152.03, -1553.06) * mm});
            skSolve(sketch);
        }
        {
            var Q0;
            Q0 = qSketchRegion(id + "F26", true);
            extrude(context, id + "F27", {"entities" : qUnion([Q0]), "operationType" : NewBodyOperationType.REMOVE, "endBound" : BoundingType.THROUGH_ALL, "oppositeDirection" : true, "depth" : 25.4 * mm, "offsetDistance" : 25.4 * mm});
        }
        {
            var Q0;
            Q0=makeQuery(id+"F1.opExtrude","SWEPT_FACE",FACE,{"disambiguationData":[OSD([sQuery(id+"F0.wireOp",EDGE,"E5")])]});
            var sketch = newSketch(context, id + "F28", { "sketchPlane" : qUnion([Q0])});
            skLineSegment(sketch, "E98.bottom", {"start": v(25576.05, -20230.84) * mm, "end": v(-8801.37, -20230.84) * mm});
            skLineSegment(sketch, "E98.top", {"start": v(25576.05, 9599.17) * mm, "end": v(-8801.37, 9599.17) * mm});
            skLineSegment(sketch, "E98.left", {"start": v(25576.05, -20230.84) * mm, "end": v(25576.05, 9599.17) * mm});
            skLineSegment(sketch, "E98.right", {"start": v(-8801.37, -20230.84) * mm, "end": v(-8801.37, 9599.17) * mm});
            skPoint(sketch, "E98.middle", {"position": v(8387.34, -5315.84) * mm});
            skSolve(sketch);
        }
        {
            var Q0;
            Q0 = qSketchRegion(id + "F28", true);
            extrude(context, id + "F29", {"entities" : qUnion([Q0]), "depth" : 457.2 * mm, "offsetDistance" : 25.4 * mm});
        }
    });
